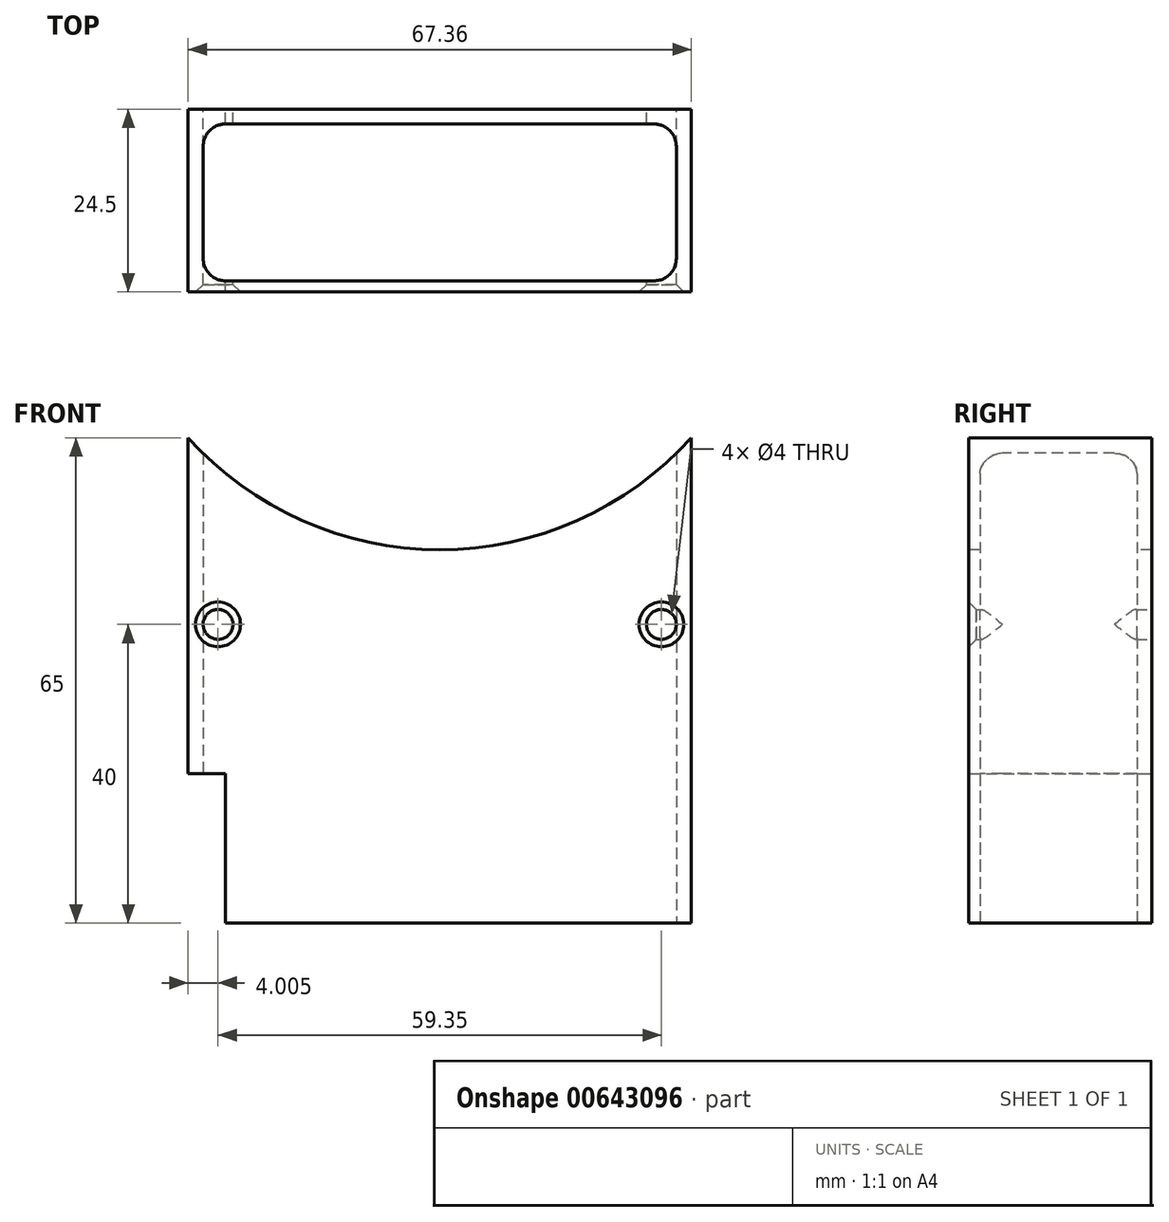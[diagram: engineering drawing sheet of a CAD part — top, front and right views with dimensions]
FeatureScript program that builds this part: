
annotation { "Feature Type Name" : "Feature", "Feature Type Description" : "" }
export const myFeature = defineFeature(function(context is Context, id is Id, definition is map)
    precondition{}
    {
        {
            var Q0;
            Q0=qCreatedBy(makeId("Top.planeOp"),FACE);
            var sketch = newSketch(context, id + "F0", { "sketchPlane" : qUnion([Q0])});
            skPoint(sketch, "E0.middle", {"position": v(0, 0) * mm});
            skLineSegment(sketch, "E1.bottom", {"start": v(28.68, 10.5) * mm, "end": v(-28.68, 10.5) * mm});
            skLineSegment(sketch, "E1.top", {"start": v(28.68, -10.5) * mm, "end": v(21.68, -10.5) * mm});
            skLineSegment(sketch, "E1.left", {"start": v(31.68, 7.5) * mm, "end": v(31.68, -7.5) * mm});
            skLineSegment(sketch, "E1.right", {"start": v(-31.68, 7.5) * mm, "end": v(-31.68, -7.5) * mm});
            skLineSegment(sketch, "E2.trimOffspring", {"start": v(-21.68, -10.5) * mm, "end": v(-28.68, -10.5) * mm});
            skPoint(sketch, "E3.visualSharp", {"position": v(-31.68, 10.5) * mm});
            skArc(sketch, "E3.filletArc", {"start": v(-28.68, 10.5) * mm, "mid": v(-30.8, 9.62) * mm, "end": v(-31.68, 7.5) * mm});
            skPoint(sketch, "E4.visualSharp", {"position": v(31.68, 10.5) * mm});
            skArc(sketch, "E4.filletArc", {"start": v(31.68, 7.5) * mm, "mid": v(30.8, 9.62) * mm, "end": v(28.68, 10.5) * mm});
            skPoint(sketch, "E5.visualSharp", {"position": v(31.68, -10.5) * mm});
            skArc(sketch, "E5.filletArc", {"start": v(28.68, -10.5) * mm, "mid": v(30.8, -9.62) * mm, "end": v(31.68, -7.5) * mm});
            skPoint(sketch, "E6.visualSharp", {"position": v(-31.68, -10.5) * mm});
            skArc(sketch, "E6.filletArc", {"start": v(-31.68, -7.5) * mm, "mid": v(-30.8, -9.62) * mm, "end": v(-28.68, -10.5) * mm});
            skLineSegment(sketch, "E7", {"start": v(-21.68, -12) * mm, "end": v(-33.68, -12) * mm});
            skLineSegment(sketch, "E8", {"start": v(-33.68, -12) * mm, "end": v(-33.68, 12.5) * mm});
            skLineSegment(sketch, "E9", {"start": v(-33.68, 12.5) * mm, "end": v(33.68, 12.5) * mm});
            skLineSegment(sketch, "E10", {"start": v(33.68, 12.5) * mm, "end": v(33.68, -12) * mm});
            skLineSegment(sketch, "E11", {"start": v(21.68, -12) * mm, "end": v(33.68, -12) * mm});
            skPoint(sketch, "E12.visualSharp", {"position": v(-33.68, 12.5) * mm});
            skLineSegment(sketch, "E12.filletArc", {"start": v(-33.68, 12.5) * mm, "end": v(-33.68, 12.5) * mm});
            skPoint(sketch, "E13.visualSharp", {"position": v(33.68, 12.5) * mm});
            skLineSegment(sketch, "E13.filletArc", {"start": v(33.68, 12.5) * mm, "end": v(33.68, 12.5) * mm});
            skPoint(sketch, "E14.visualSharp", {"position": v(33.68, -12) * mm});
            skLineSegment(sketch, "E14.filletArc", {"start": v(33.68, -12) * mm, "end": v(33.68, -12) * mm});
            skPoint(sketch, "E15.visualSharp", {"position": v(-33.68, -12) * mm});
            skLineSegment(sketch, "E15.filletArc", {"start": v(-33.68, -12) * mm, "end": v(-33.68, -12) * mm});
            skLineSegment(sketch, "E16", {"start": v(-21.68, -10.5) * mm, "end": v(21.68, -10.5) * mm});
            skLineSegment(sketch, "E17", {"start": v(21.68, -12) * mm, "end": v(-21.68, -12) * mm});
            skSolve(sketch);
        }
        {
            var Q0;
            Q0=makeQuery(id+"F0.imprint","IMPRINT",FACE,{"disambiguationData":[TD([[makeQuery(id+"F0.imprint","IMPRINT",EDGE,{"derivedFrom":sQuery(id+"F0.wireOp",EDGE,"E1.bottom")}),-1.0]])]});
            extrude(context, id + "F1", {"entities" : qUnion([Q0]), "depth" : 65 * mm, "offsetDistance" : 25 * mm});
        }
        {
            var Q0;
            Q0=qCreatedBy(makeId("Front.planeOp"),FACE);
            var sketch = newSketch(context, id + "F2", { "sketchPlane" : qUnion([Q0])});
            skLineSegment(sketch, "E18", {"start": v(33.68, 65) * mm, "end": v(-33.68, 65) * mm});
            skArc(sketch, "E19", {"start": v(-33.68, 65) * mm, "mid": v(0, 50) * mm, "end": v(33.68, 65) * mm});
            skSolve(sketch);
        }
        {
            var Q0;
            Q0=qSketchRegion(id+"F2",true);
            extrude(context, id + "F3", {"entities" : qUnion([Q0]), "operationType" : NewBodyOperationType.REMOVE, "endBound" : BoundingType.SYMMETRIC, "oppositeDirection" : true, "depth" : 50 * mm, "offsetDistance" : 25 * mm});
        }
        {
            var Q0;
            Q0=makeQuery(id+"F1.opExtrude","SWEPT_FACE",FACE,{"disambiguationData":[OSD([sQuery(id+"F0.wireOp",EDGE,"E8")])]});
            var sketch = newSketch(context, id + "F4", { "sketchPlane" : qUnion([Q0])});
            skPoint(sketch, "E20.middle", {"position": v(0, 0) * mm});
            skLineSegment(sketch, "E21.bottom", {"start": v(26.53, 20) * mm, "end": v(-26.53, 20) * mm});
            skLineSegment(sketch, "E21.top", {"start": v(26.53, -20) * mm, "end": v(-26.53, -20) * mm});
            skLineSegment(sketch, "E21.left", {"start": v(26.53, 20) * mm, "end": v(26.53, -20) * mm});
            skLineSegment(sketch, "E21.right", {"start": v(-26.53, 20) * mm, "end": v(-26.53, -20) * mm});
            skSolve(sketch);
        }
        {
            var Q0;
            Q0=qSketchRegion(id+"F4",true);
            var Q1;
            Q1=makeQuery(id+"F1.opExtrude","SWEPT_FACE",FACE,{"disambiguationData":[OSD([sQuery(id+"F0.wireOp",EDGE,"E1.right")])]});
            var Q2;
            Q2=makeQuery(id+"F1.opExtrude","CAP_VERTEX",VERTEX,{"disambiguationData":[OSD([sQuery(id+"F0.wireOp",EDGE,"E1.bottom"),sQuery(id+"F0.wireOp",EDGE,"E3.filletArc")])],"isStart":true});
            extrude(context, id + "F5", {"entities" : qUnion([Q0]), "operationType" : NewBodyOperationType.REMOVE, "endBound" : BoundingType.UP_TO_VERTEX, "oppositeDirection" : true, "depth" : 25 * mm, "endBoundEntityFace" : qUnion([Q1]), "endBoundEntityVertex" : qUnion([Q2]), "offsetDistance" : 25 * mm});
        }
        {
            var Q0;
            Q0=makeQuery(id+"F1.opExtrude","SWEPT_FACE",FACE,{"disambiguationData":[OSD([sQuery(id+"F0.wireOp",EDGE,"E9")])]});
            var sketch = newSketch(context, id + "F6", { "sketchPlane" : qUnion([Q0])});
            skCircle(sketch, "E22", {"center": v(29.67, 40) * mm, "radius": 2 * mm});
            skCircle(sketch, "E23", {"center": v(-29.68, 40) * mm, "radius": 2 * mm});
            skSolve(sketch);
        }
        {
            var Q0;
            Q0 = qSketchRegion(id + "F6", true);
            extrude(context, id + "F7", {"entities" : qUnion([Q0]), "operationType" : NewBodyOperationType.REMOVE, "endBound" : BoundingType.THROUGH_ALL, "oppositeDirection" : true, "depth" : 25 * mm, "offsetDistance" : 25 * mm});
        }
        {
            var Q0;
            Q0=makeQuery(id+"F7.boolean.opBoolean","INTERSECT",EDGE,{"derivedFrom":[makeQuery(id+"F1.opExtrude","SWEPT_FACE",FACE,{"disambiguationData":[OSD([sQuery(id+"F0.wireOp",EDGE,"E7"),sQuery(id+"F0.wireOp",EDGE,"E11"),sQuery(id+"F0.wireOp",EDGE,"E17")])]}),makeQuery(id+"F7.opExtrude","SWEPT_FACE",FACE,{"disambiguationData":[OSD([sQuery(id+"F6.wireOp",EDGE,"E22")])]})]});
            var Q1;
            Q1=makeQuery(id+"F7.boolean.opBoolean","INTERSECT",EDGE,{"derivedFrom":[makeQuery(id+"F1.opExtrude","SWEPT_FACE",FACE,{"disambiguationData":[OSD([sQuery(id+"F0.wireOp",EDGE,"E7"),sQuery(id+"F0.wireOp",EDGE,"E11"),sQuery(id+"F0.wireOp",EDGE,"E17")])]}),makeQuery(id+"F7.opExtrude","SWEPT_FACE",FACE,{"disambiguationData":[OSD([sQuery(id+"F6.wireOp",EDGE,"E23")])]})]});
            chamfer(context, id + "F8", {"entities" : qUnion([Q0, Q1]), "chamferType" : ChamferType.OFFSET_ANGLE, "width" : 1 * mm, "oppositeDirection" : false, "angle" : 45 * degree, "tangentPropagation" : true});
        }
    });
